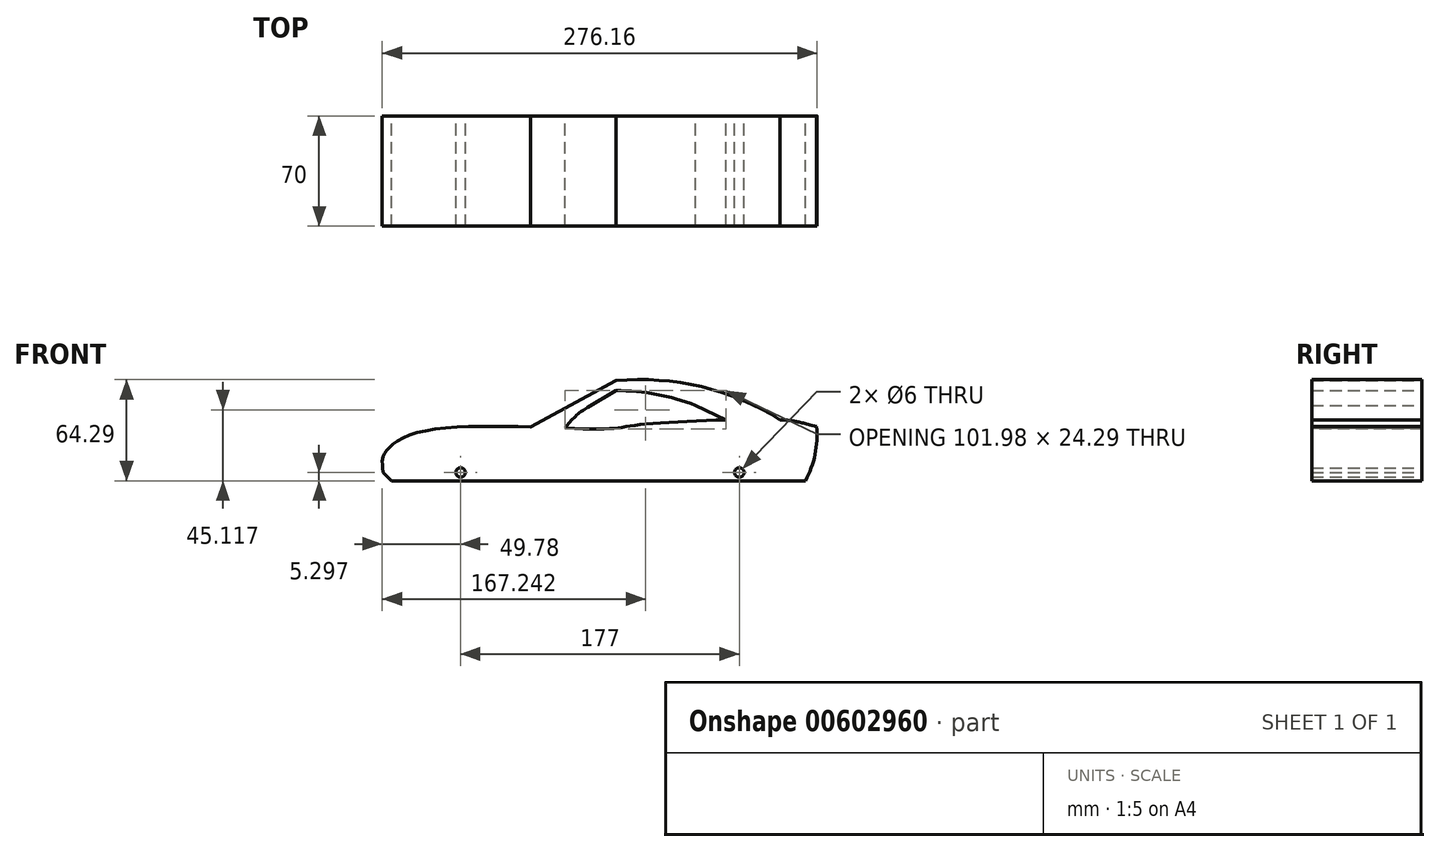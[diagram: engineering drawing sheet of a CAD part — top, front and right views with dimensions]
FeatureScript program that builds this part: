
annotation { "Feature Type Name" : "Feature", "Feature Type Description" : "" }
export const myFeature = defineFeature(function(context is Context, id is Id, definition is map)
    precondition{}
    {
        {
            var Q0;
            Q0=qCreatedBy(makeId("Front.planeOp"),FACE);
            var sketch = newSketch(context, id + "F0", { "sketchPlane" : qUnion([Q0])});
            skLineSegment(sketch, "E0", {"start": v(-65.5, 0) * mm, "end": v(65.5, 0) * mm});
            skLineSegment(sketch, "E1", {"start": v(-111.5, 0) * mm, "end": v(-132.5, 0) * mm});
            skLineSegment(sketch, "E2", {"start": v(111.5, 0) * mm, "end": v(130.5, 0) * mm});
            skLineSegment(sketch, "E3", {"start": v(-132.5, 0) * mm, "end": v(-137.7, 5.3) * mm});
            skLineSegment(sketch, "E4", {"start": v(-137.7, 5.3) * mm, "end": v(-110.88, 5.3) * mm});
            skLineSegment(sketch, "E5", {"start": v(-66.12, 5.3) * mm, "end": v(66.12, 5.3) * mm});
            skPoint(sketch, "E5.startSnap0", {"position": v(-124.29, 5.3) * mm});
            skFitSpline(sketch, "E6", {"points": [v(-137.7, 5.3) * mm, v(-137.7, 15.48) * mm, v(-116.35, 30.52) * mm, v(0, 32.94) * mm, v(27.2, 35.85) * mm, v(114.5, 38.76) * mm, v(137.63, 34.4) * mm], "startDerivative": vector(-16.15, 189.72) * mm, "endDerivative": vector(280.44, -70.02) * mm});
            skLineSegment(sketch, "E7", {"start": v(-7.76, 46.71) * mm, "end": v(10.23, 57.26) * mm});
            skLineSegment(sketch, "E8", {"start": v(-44.12, 34.24) * mm, "end": v(10.23, 63.57) * mm});
            skArc(sketch, "E9", {"start": v(114.5, 38.76) * mm, "mid": v(64.4, 59.75) * mm, "end": v(10.23, 63.57) * mm});
            skPoint(sketch, "E10.endSnap0", {"position": v(-16.94, 48.9) * mm});
            skArc(sketch, "E11", {"start": v(60.72, 47.89) * mm, "mid": v(35.92, 54.96) * mm, "end": v(10.23, 57.26) * mm});
            skArc(sketch, "E12", {"start": v(-7.76, 46.71) * mm, "mid": v(-15.62, 40.86) * mm, "end": v(-22.03, 33.45) * mm});
            skLineSegment(sketch, "E13", {"start": v(60.72, 47.89) * mm, "end": v(79.95, 38.68) * mm});
            skArc(sketch, "E14", {"start": v(130.5, 0) * mm, "mid": v(136.62, 16.67) * mm, "end": v(137.63, 34.4) * mm});
            skLineSegment(sketch, "E15", {"start": v(110.88, 5.3) * mm, "end": v(133.06, 5.3) * mm});
            skLineSegment(sketch, "E16", {"start": v(-111.5, 0) * mm, "end": v(-65.5, 0) * mm});
            skLineSegment(sketch, "E17", {"start": v(65.5, 0) * mm, "end": v(111.5, 0) * mm});
            skCircle(sketch, "E18", {"center": v(-88.5, 5.3) * mm, "radius": 3 * mm});
            skPoint(sketch, "E18.centerSnap0", {"position": v(-88.5, 0) * mm});
            skCircle(sketch, "E19", {"center": v(88.5, 5.3) * mm, "radius": 3 * mm});
            skPoint(sketch, "E19.centerSnap0", {"position": v(88.5, 0) * mm});
            skCircle(sketch, "E20", {"center": v(-88.5, 5.3) * mm, "radius": 18.5 * mm, "construction": true});
            skCircle(sketch, "E21", {"center": v(88.5, 5.3) * mm, "radius": 18.5 * mm, "construction": true});
            skSolve(sketch);
        }
        {
            var Q0;
            Q0 = qSketchRegion(id + "F0", true);
            extrude(context, id + "F1", {"entities" : qUnion([Q0]), "depth" : 70 * mm, "offsetDistance" : 25 * mm});
        }
    });
